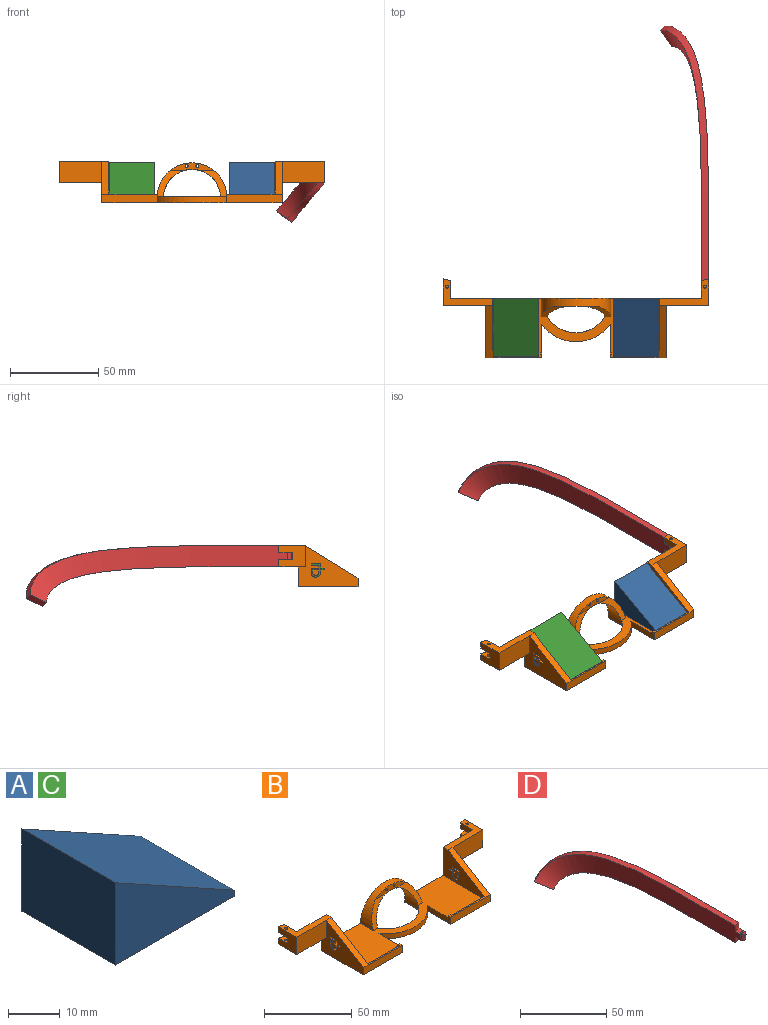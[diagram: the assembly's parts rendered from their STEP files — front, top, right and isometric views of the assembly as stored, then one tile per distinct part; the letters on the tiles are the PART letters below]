
ASSEMBLY  parts=4 mates=3
PART A: 6 faces, bbox 32.5x25.5x19.5 mm
  f0: plane 25.5x1.5mm, normal (1,0,0), area 38.2mm2, adj f1,f3,f4,f5
  f1: plane 32.5x25.5mm, normal (0.48,0,0.87), area 947.4mm2, adj f0,f2,f4,f5
  f2: plane 25.5x19.5mm, normal (-1,0,0), area 497.2mm2, adj f1,f3,f4,f5
  f3: plane 32.5x25.5mm, normal (0,0,-1), area 828.8mm2, adj f0,f2,f4,f5
  f4: plane 32.5x19.5mm, normal (0,1,0), area 341.3mm2, adj f0,f1,f2,f3
  f5: plane 32.5x19.5mm, normal (0,-1,0), area 341.3mm2, adj f0,f1,f2,f3
PART B: 113 faces, bbox 150x44.8x23.3 mm
  f0: plane 15x12mm, normal (1,0,0), area 150mm2, adj f2,f3,f8,f24,f26,f104,f105,f106
  f1: plane 12x9.93mm, normal (-1,0,0), area 93.4mm2, adj f2,f3,f8,f17,f24,f104,f105,f106
  f2: plane 4x4mm, normal (-0.26,0.97,0), area 16.6mm2, adj f0,f1,f24,f104
  f3: plane 4x4mm, normal (-0.26,0.97,0), area 16.6mm2, adj f0,f1,f8,f105
  f4: plane 12x9.93mm, normal (1,0,0), area 93.4mm2, adj f6,f7,f17,f35,f100,f101,f102,f103
  f5: plane 15x12mm, normal (-1,0,0), area 150mm2, adj f6,f7,f34,f35,f100,f101,f102,f103
  f6: plane 4x4mm, normal (0.26,0.97,0), area 16.6mm2, adj f4,f5,f7,f101
  f7: plane 28x15mm, normal (0,0,1), area 151.8mm2, adj f4,f5,f6,f15,f17,f33,f34,f112
  f8: plane 24x15mm, normal (0,0,-1), area 137.9mm2, adj f0,f1,f3,f12,f17,f26
  f9: cylinder r=19.5mm len=32.44mm, axis (0,0,1), area 114.5mm2, adj f11,f92,f97,f98,f99
  f10: plane 24.14x4.13mm, normal (0,-1,0), area 62.6mm2, adj f91,f92,f93,f94,f95,f96
  f11: plane 94x32.75mm, normal (0,0,1), area 2014.7mm2, adj f9,f13,f15,f17,f18,f19,f21,f22
  f12: plane 33.75x23.25mm, normal (1,0,0), area 443.3mm2, adj f8,f16,f17,f20,f25,f26,f65,f66
  f13: plane 33.75x19.75mm, normal (-1,0,0), area 371.7mm2, adj f11,f17,f21,f23,f24,f25,f65,f66
  f14: plane 33.75x23.25mm, normal (-1,0,0), area 442.6mm2, adj f17,f20,f28,f33,f34,f35,f37,f38
  f15: plane 33.75x19.75mm, normal (1,0,0), area 371mm2, adj f7,f11,f17,f30,f32,f33,f37,f38
  f16: plane 31.5x5mm, normal (0,-1,0), area 157.5mm2, adj f12,f19,f20,f23,f25
  f17: plane 142x23.25mm, normal (0,1,0), area 1079.5mm2, adj f1,f4,f7,f8,f11,f12,f13,f14
  f18: cylinder r=24.5mm len=39mm, axis (0,0,1), area 157.9mm2, adj f11,f19,f20,f29
  f19: plane 18.92x5mm, normal (-1,0,0), area 70mm2, adj f11,f16,f18,f20,f23,f27
  f20: plane 102x33.75mm, normal (0,0,-1), area 2391.7mm2, adj f12,f14,f16,f17,f18,f19,f28,f29
  f21: plane 26x1.5mm, normal (0,1,0), area 39mm2, adj f11,f13,f22,f23
  f22: plane 2x1.5mm, normal (1,0,0), area 2.3mm2, adj f11,f21,f23,f27
  f23: plane 27.5x2mm, normal (0,0,1), area 29mm2, adj f13,f16,f19,f21,f22,f27
  f24: plane 28x15mm, normal (0,0,1), area 151.8mm2, adj f0,f1,f2,f13,f17,f25,f26,f109
  f25: plane 29.75x18.25mm, normal (0,-0.52,0.85), area 139.6mm2, adj f12,f13,f16,f24
  f26: plane 24x12mm, normal (0,-1,0), area 288mm2, adj f0,f8,f12,f24
  f27: plane 1.5x1.5mm, normal (0,0.83,0.55), area 2.7mm2, adj f11,f19,f22,f23
  f28: plane 31.5x5mm, normal (0,-1,0), area 157.5mm2, adj f14,f20,f29,f32,f33
  f29: plane 18.92x5mm, normal (1,0,0), area 70mm2, adj f11,f18,f20,f28,f32,f36
  f30: plane 26x1.5mm, normal (0,1,0), area 39mm2, adj f11,f15,f31,f32
  f31: plane 2x1.5mm, normal (-1,0,0), area 2.3mm2, adj f11,f30,f32,f36
  f32: plane 27.5x2mm, normal (0,0,1), area 29mm2, adj f15,f28,f29,f30,f31,f36
  f33: plane 29.75x18.25mm, normal (0,-0.52,0.85), area 139.6mm2, adj f7,f14,f15,f28
  f34: plane 24x12mm, normal (0,-1,0), area 288mm2, adj f5,f7,f14,f35
  f35: plane 24x15mm, normal (0,0,-1), area 137.9mm2, adj f4,f5,f14,f17,f34,f100
  f36: plane 1.5x1.5mm, normal (0,0.83,0.55), area 2.7mm2, adj f11,f29,f31,f32
  f37: cylinder r=2.67mm len=4mm, axis (-1,0,0), area 4.1mm2, adj f14,f15,f38,f50
  f38: plane 4x1.5mm, normal (0,1,0), area 6mm2, adj f14,f15,f37,f39
  f39: plane 4x2.17mm, normal (0,0,1), area 8.7mm2, adj f14,f15,f38,f40
  f40: plane 4x1mm, normal (0,1,0), area 4mm2, adj f14,f15,f39,f41
  f41: plane 4x2.17mm, normal (0,0,-1), area 8.7mm2, adj f14,f15,f40,f42
  f42: plane 4x2.5mm, normal (0,1,0), area 10mm2, adj f14,f15,f41,f43
  f43: plane 5.33x4mm, normal (0,0,-1), area 21.3mm2, adj f14,f15,f42,f44
  f44: plane 4x1mm, normal (0,-1,0), area 4mm2, adj f14,f15,f43,f45
  f45: plane 4.33x4mm, normal (0,0,1), area 17.3mm2, adj f14,f15,f44,f46
  f46: plane 4x1.5mm, normal (0,-1,0), area 6mm2, adj f14,f15,f45,f47
  f47: plane 4x1.42mm, normal (0,0,-1), area 5.7mm2, adj f14,f15,f46,f48
  f48: plane 4x1mm, normal (0,-1,0), area 4mm2, adj f14,f15,f47,f49
  f49: plane 4x1.42mm, normal (0,0,1), area 5.7mm2, adj f14,f15,f48,f51
  f50: plane 4x0.88mm, normal (0,-0.5,0.87), area 4.1mm2, adj f14,f15,f37,f52
  f51: plane 4x1.5mm, normal (0,-1,0), area 6mm2, adj f14,f15,f49,f52
  f52: cylinder r=1.67mm len=4mm, axis (-1,0,0), area 2mm2, adj f14,f15,f50,f51
  f53: plane 4x0.87mm, normal (0,-0.5,-0.87), area 4mm2, adj f14,f15,f54,f55
  f54: cylinder r=1.67mm len=4mm, axis (-1,0,0), area 13mm2, adj f14,f15,f53,f56
  f55: cylinder r=2.67mm len=4.49mm, axis (-1,0,0), area 21.3mm2, adj f14,f15,f53,f56
  f56: plane 4x0.87mm, normal (0,0.5,-0.87), area 4mm2, adj f14,f15,f54,f55
  f57: cylinder r=1.67mm len=4mm, axis (-1,0,0), area 2mm2, adj f14,f15,f58,f63
  f58: plane 4x1.5mm, normal (0,1,0), area 6mm2, adj f14,f15,f57,f59
  f59: plane 4x1.42mm, normal (0,0,1), area 5.7mm2, adj f14,f15,f58,f60
  f60: plane 4x1mm, normal (0,1,0), area 4mm2, adj f14,f15,f59,f61
  f61: plane 4x2.42mm, normal (0,0,-1), area 9.7mm2, adj f14,f15,f60,f62
  f62: plane 4x2.5mm, normal (0,-1,0), area 10mm2, adj f14,f15,f61,f64
  f63: plane 4x0.88mm, normal (0,0.5,0.87), area 4.1mm2, adj f14,f15,f57,f64
  f64: cylinder r=2.67mm len=4mm, axis (-1,0,0), area 4.1mm2, adj f14,f15,f62,f63
  f65: cylinder r=2.67mm len=4mm, axis (1,0,0), area 4.1mm2, adj f12,f13,f66,f78
  f66: plane 4x1.5mm, normal (0,-1,0), area 6mm2, adj f12,f13,f65,f67
  f67: plane 4x2.17mm, normal (0,0,1), area 8.7mm2, adj f12,f13,f66,f68
  f68: plane 4x1mm, normal (0,-1,0), area 4mm2, adj f12,f13,f67,f69
  f69: plane 4x2.17mm, normal (0,0,-1), area 8.7mm2, adj f12,f13,f68,f70
  f70: plane 4x2.5mm, normal (0,-1,0), area 10mm2, adj f12,f13,f69,f71
  f71: plane 5.33x4mm, normal (0,0,-1), area 21.3mm2, adj f12,f13,f70,f72
  f72: plane 4x1mm, normal (0,1,0), area 4mm2, adj f12,f13,f71,f73
  f73: plane 4.33x4mm, normal (0,0,1), area 17.3mm2, adj f12,f13,f72,f74
  f74: plane 4x1.5mm, normal (0,1,0), area 6mm2, adj f12,f13,f73,f75
  f75: plane 4x1.42mm, normal (0,0,-1), area 5.7mm2, adj f12,f13,f74,f76
  f76: plane 4x1mm, normal (0,1,0), area 4mm2, adj f12,f13,f75,f77
  f77: plane 4x1.42mm, normal (0,0,1), area 5.7mm2, adj f12,f13,f76,f79
  f78: plane 4x0.88mm, normal (0,0.5,0.87), area 4.1mm2, adj f12,f13,f65,f80
  f79: plane 4x1.5mm, normal (0,1,0), area 6mm2, adj f12,f13,f77,f80
  f80: cylinder r=1.67mm len=4mm, axis (1,0,0), area 2mm2, adj f12,f13,f78,f79
  f81: plane 4x1mm, normal (0,-1,0), area 4mm2, adj f12,f13,f82,f84
  f82: plane 4x2.42mm, normal (0,0,-1), area 9.7mm2, adj f12,f13,f81,f83
  f83: plane 4x2.5mm, normal (0,1,0), area 10mm2, adj f12,f13,f82,f85
  f84: plane 4x1.42mm, normal (0,0,1), area 5.7mm2, adj f12,f13,f81,f86
  f85: plane 4x1mm, normal (0,0,1), area 4mm2, adj f12,f13,f83,f86
  f86: plane 4x1.5mm, normal (0,-1,0), area 6mm2, adj f12,f13,f84,f85
  f87: plane 4x0.87mm, normal (0,0.5,-0.87), area 4mm2, adj f12,f13,f88,f89
  f88: cylinder r=1.67mm len=4mm, axis (1,0,0), area 13mm2, adj f12,f13,f87,f90
  f89: cylinder r=2.67mm len=4.49mm, axis (1,0,0), area 21.3mm2, adj f12,f13,f87,f90
  f90: plane 4x0.87mm, normal (0,-0.5,-0.87), area 4mm2, adj f12,f13,f88,f89
  f91: cylinder r=19.72mm len=39.41mm, axis (0,1,0), area 369.8mm2, adj f10,f11,f17,f95,f96
  f92: cylinder r=16.22mm len=32.44mm, axis (0,1,0), area 388.5mm2, adj f9,f10,f11,f17,f95,f96,f97,f99
  f93: cylinder r=0.75mm len=4.5mm, axis (0,1,0), area 21.2mm2, adj f10,f17
  f94: cylinder r=0.75mm len=4.5mm, axis (0,1,0), area 21.2mm2, adj f10,f17
  f95: plane 16.22x15mm, normal (0,-0.93,0.37), area 72.8mm2, adj f10,f11,f91,f92
  f96: plane 16.22x15mm, normal (0,-0.93,0.37), area 72.8mm2, adj f10,f11,f91,f92
  f97: cylinder r=0.5mm len=11.19mm, axis (0,1,0), area 9.4mm2, adj f9,f17,f20,f92,f98
  f98: torus R=20mm, axis (0,0,1), area 30.1mm2, adj f9,f20,f97,f99
  f99: cylinder r=0.5mm len=11.19mm, axis (0,1,0), area 9.4mm2, adj f9,f17,f20,f92,f98
  f100: plane 4x4mm, normal (0.26,0.97,0), area 16.6mm2, adj f4,f5,f35,f102
  f101: plane 7.5x4mm, normal (0,0,-1), area 25.8mm2, adj f4,f5,f6,f103,f112
  f102: plane 7.5x4mm, normal (0,0,1), area 25.8mm2, adj f4,f5,f100,f103,f111
  f103: plane 4x4mm, normal (0,1,0), area 16mm2, adj f4,f5,f101,f102
  f104: plane 7.5x4mm, normal (0,0,-1), area 25.8mm2, adj f0,f1,f2,f106,f109
  f105: plane 7.5x4mm, normal (0,0,1), area 25.8mm2, adj f0,f1,f3,f106,f108
  f106: plane 4x4mm, normal (0,1,0), area 16mm2, adj f0,f1,f104,f105
  f107: plane 1.6x1.6mm, normal (0,0,1), area 2mm2, adj f108
  f108: cylinder r=0.8mm len=2mm, axis (0,0,1), area 10.1mm2, adj f105,f107
  f109: cylinder r=0.8mm len=4mm, axis (0,0,1), area 20.1mm2, adj f24,f104
  f110: plane 1.6x1.6mm, normal (0,0,1), area 2mm2, adj f111
  f111: cylinder r=0.8mm len=2mm, axis (0,0,1), area 10.1mm2, adj f102,f110
  f112: cylinder r=0.8mm len=4mm, axis (0,0,1), area 20.1mm2, adj f7,f101
PART C: same geometry as A
PART D: 12 faces, bbox 27.6x150.3x34.8 mm
  f0: bspline ~150.25x34.73mm, area 1868.9mm2, adj f1,f2,f4,f5,f6,f8,f9,f11
  f1: bspline ~144.16x30.11mm, area 640.5mm2, adj f0,f3,f4,f8
  f2: bspline ~140.97x22.68mm, area 579.4mm2, adj f0,f3,f4,f9
  f3: bspline ~145.55x32.21mm, area 1825.9mm2, adj f1,f2,f4,f5,f6,f8,f9,f10
  f4: plane 11.73x8.66mm, normal (-0.64,-0.09,-0.76), area 48mm2, adj f0,f1,f2,f3
  f5: plane 6.94x4.07mm, normal (0,0,-1), area 21.9mm2, adj f0,f3,f7,f9,f10,f11
  f6: plane 7.08x4.06mm, normal (0,0,1), area 22.2mm2, adj f0,f3,f7,f8,f10,f11
  f7: cylinder r=0.8mm len=4mm, axis (0,0,1), area 20.1mm2, adj f5,f6
  f8: plane 4.02x4.01mm, normal (0.26,-0.97,0), area 16.6mm2, adj f0,f1,f3,f6
  f9: plane 4.01x4.01mm, normal (0.23,-0.97,0), area 16.4mm2, adj f0,f2,f3,f5
  f10: bspline ~6.84x2mm, area 12.6mm2, adj f3,f5,f6,f11
  f11: bspline ~4x2mm, area 12.6mm2, adj f0,f5,f6,f10
PLACE A rot(axis=(0,0,-1),90deg) t=(35.36,-52.28,100.25)mm
PLACE B t=(1.36,-35.78,100.25)mm
PLACE C rot(axis=(0,0,-1),90deg) t=(-32.64,-52.28,100.25)mm
PLACE D t=(76.36,-31.78,120)mm
MATE revolute D.f7 <-> B.f108  axis (0,0,-1) through (74.36,-29.28,112)mm
MATE fastened C.f0 <-> B.f30  axis (0,-1,0) through (-32.64,-68.53,101)mm
MATE fastened A.f0 <-> B.f21  axis (0,-1,0) through (35.36,-68.53,101)mm
